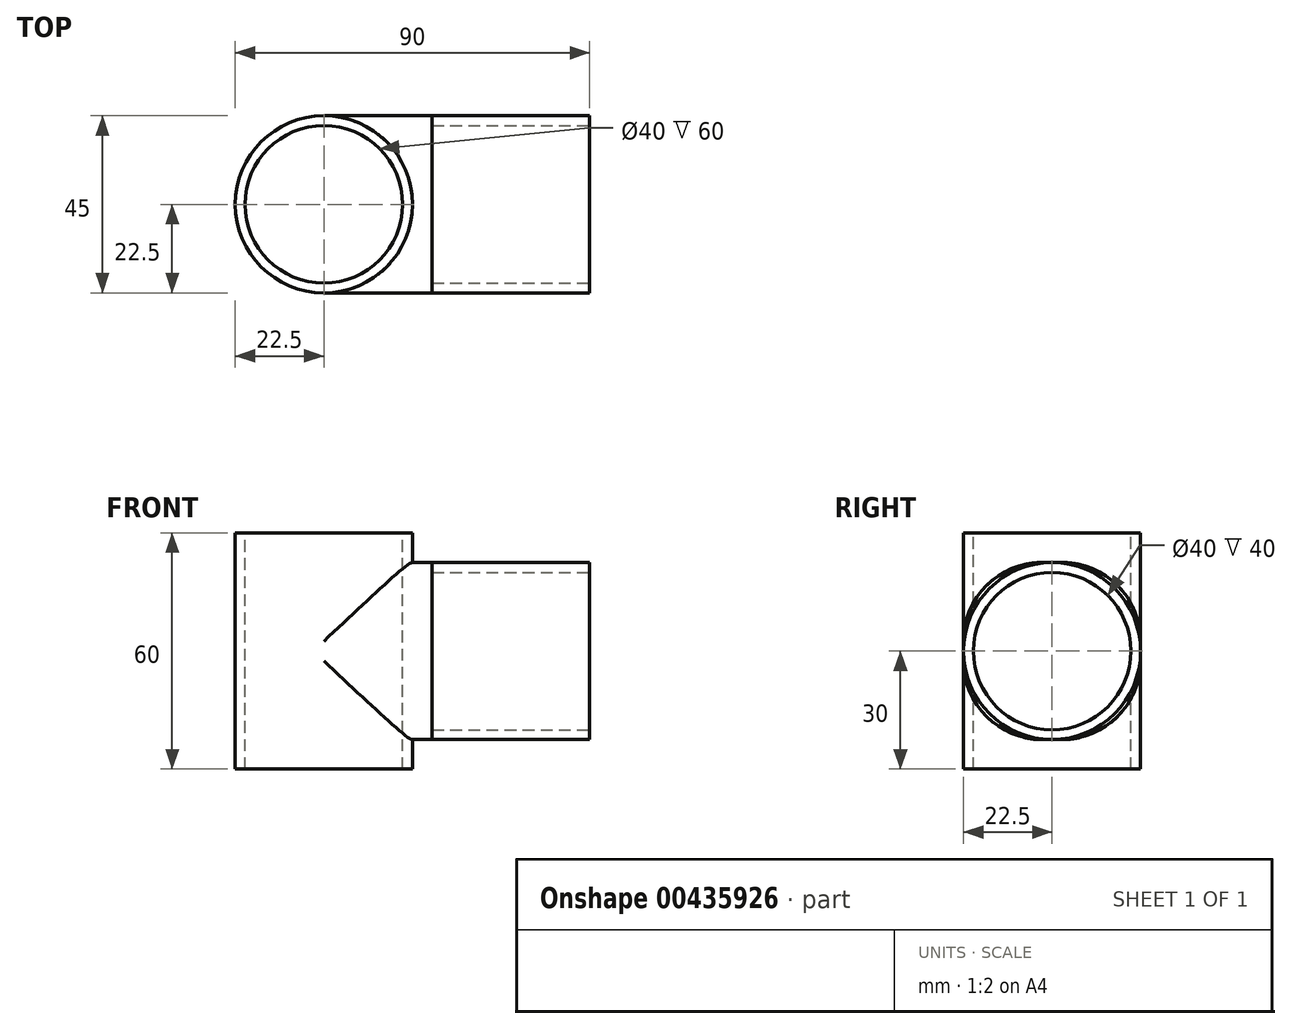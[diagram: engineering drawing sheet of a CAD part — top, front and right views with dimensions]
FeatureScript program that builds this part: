
annotation { "Feature Type Name" : "Feature", "Feature Type Description" : "" }
export const myFeature = defineFeature(function(context is Context, id is Id, definition is map)
    precondition{}
    {
        {
            var Q0;
            Q0=qCreatedBy(makeId("Top.planeOp"),FACE);
            var sketch = newSketch(context, id + "F0", { "sketchPlane" : qUnion([Q0])});
            skCircle(sketch, "E0", {"center": v(0, 0) * mm, "radius": 22.5 * mm});
            skLineSegment(sketch, "E1", {"start": v(0, 22.5) * mm, "end": v(67.5, 22.5) * mm});
            skLineSegment(sketch, "E2", {"start": v(67.5, -22.5) * mm, "end": v(0, -22.5) * mm});
            skLineSegment(sketch, "E3", {"start": v(67.5, 22.5) * mm, "end": v(67.5, -22.5) * mm});
            skSolve(sketch);
        }
        {
            var Q0;
            {var subQ0=sQuery(id+"F0.wireOp",EDGE,"E1");Q0=makeQuery(id+"F0.imprint","IMPRINT",FACE,{"disambiguationData":[TD([[makeQuery(id+"F0.imprint","IMPRINT",EDGE,{"derivedFrom":subQ0}),-1.0]])]});}
            extrude(context, id + "F1", {"entities" : qUnion([Q0]), "endBound" : BoundingType.SYMMETRIC, "depth" : 45 * mm});
        }
        {
            var Q0;
            {var subQ0=sQuery(id+"F0.wireOp",EDGE,"E0");var subQ1=makeQuery(id+"F0.imprint","INTERSECT",VERTEX,{"derivedFrom":[subQ0,sQuery(id+"F0.wireOp",EDGE,"E1")]});Q0=makeQuery(id+"F0.imprint","IMPRINT",FACE,{"disambiguationData":[TD([[makeQuery(id+"F0.imprint","IMPRINT",EDGE,{"disambiguationData":[TD([[subQ1,-1.0]])],"derivedFrom":subQ0}),1.0]])]});}
            extrude(context, id + "F2", {"entities" : qUnion([Q0]), "operationType" : NewBodyOperationType.ADD, "endBound" : BoundingType.SYMMETRIC, "depth" : 60 * mm});
        }
        {
            var Q0;
            Q0=makeQuery(id+"F1.opExtrude","SWEPT_FACE",FACE,{"disambiguationData":[OSD([sQuery(id+"F0.wireOp",EDGE,"E3")])]});
            var sketch = newSketch(context, id + "F3", { "sketchPlane" : qUnion([Q0])});
            skCircle(sketch, "E4", {"center": v(0, 0) * mm, "radius": 22.5 * mm});
            skSolve(sketch);
        }
        {
            var Q0;
            {var subQ0=sQuery(id+"F3.wireOp",EDGE,"E4");var subQ1=sQuery(id+"F0.wireOp",EDGE,"E3");var subQ4=makeQuery(id+"F1.opExtrude","CAP_EDGE",EDGE,{"disambiguationData":[OSD([subQ1])],"isStart":true});var subQ5=makeQuery(id+"F3.imprint","INTERSECT",VERTEX,{"derivedFrom":[subQ4,subQ0]});Q0=makeQuery(id+"F3.imprint","IMPRINT",FACE,{"disambiguationData":[TD([[makeQuery(id+"F3.imprint","IMPRINT",EDGE,{"disambiguationData":[TD([[subQ5,1.0]])],"derivedFrom":subQ0}),-1.0]])]});}
            var Q1;
            {var subQ0=sQuery(id+"F3.wireOp",EDGE,"E4");var subQ1=sQuery(id+"F0.wireOp",EDGE,"E3");var subQ2=makeQuery(id+"F1.opExtrude","CAP_EDGE",EDGE,{"disambiguationData":[OSD([subQ1])],"isStart":false});var subQ3=makeQuery(id+"F3.imprint","INTERSECT",VERTEX,{"derivedFrom":[subQ2,subQ0]});Q1=makeQuery(id+"F3.imprint","IMPRINT",FACE,{"disambiguationData":[TD([[makeQuery(id+"F3.imprint","IMPRINT",EDGE,{"disambiguationData":[TD([[subQ3,-1.0]])],"derivedFrom":subQ0}),-1.0]])]});}
            var Q2;
            {var subQ0=sQuery(id+"F3.wireOp",EDGE,"E4");var subQ1=sQuery(id+"F0.wireOp",EDGE,"E3");var subQ2=makeQuery(id+"F1.opExtrude","CAP_EDGE",EDGE,{"disambiguationData":[OSD([subQ1])],"isStart":false});var subQ3=makeQuery(id+"F3.imprint","INTERSECT",VERTEX,{"derivedFrom":[subQ2,subQ0]});Q2=makeQuery(id+"F3.imprint","IMPRINT",FACE,{"disambiguationData":[TD([[makeQuery(id+"F3.imprint","IMPRINT",EDGE,{"disambiguationData":[TD([[subQ3,1.0]])],"derivedFrom":subQ0}),-1.0]])]});}
            var Q3;
            {var subQ0=sQuery(id+"F3.wireOp",EDGE,"E4");var subQ1=sQuery(id+"F0.wireOp",EDGE,"E3");var subQ4=makeQuery(id+"F1.opExtrude","CAP_EDGE",EDGE,{"disambiguationData":[OSD([subQ1])],"isStart":true});var subQ5=makeQuery(id+"F3.imprint","INTERSECT",VERTEX,{"derivedFrom":[subQ4,subQ0]});Q3=makeQuery(id+"F3.imprint","IMPRINT",FACE,{"disambiguationData":[TD([[makeQuery(id+"F3.imprint","IMPRINT",EDGE,{"disambiguationData":[TD([[subQ5,-1.0]])],"derivedFrom":subQ0}),-1.0]])]});}
            extrude(context, id + "F4", {"entities" : qUnion([Q0, Q1, Q2, Q3]), "operationType" : NewBodyOperationType.REMOVE, "oppositeDirection" : true, "depth" : 40 * mm});
        }
        {
            var Q0;
            Q0=makeQuery(id+"F1.opExtrude","CAP_EDGE",EDGE,{"disambiguationData":[OSD([sQuery(id+"F0.wireOp",EDGE,"E1")])],"isStart":false});
            var Q1;
            Q1=makeQuery(id+"F1.opExtrude","CAP_EDGE",EDGE,{"disambiguationData":[OSD([sQuery(id+"F0.wireOp",EDGE,"E1")])],"isStart":true});
            var Q2;
            Q2=makeQuery(id+"F1.opExtrude","CAP_EDGE",EDGE,{"disambiguationData":[OSD([sQuery(id+"F0.wireOp",EDGE,"E2")])],"isStart":false});
            var Q3;
            Q3=makeQuery(id+"F1.opExtrude","CAP_EDGE",EDGE,{"disambiguationData":[OSD([sQuery(id+"F0.wireOp",EDGE,"E2")])],"isStart":true});
            fillet(context, id + "F5", {"entities" : qUnion([Q0, Q1, Q2, Q3]), "radius" : 20 * mm, "tangentPropagation" : true, "allowEdgeOverflow" : false});
        }
        {
            var Q0;
            Q0=makeQuery(id+"F2.opExtrude","CAP_FACE",FACE,{"disambiguationData":[OSD([sQuery(id+"F0.wireOp",EDGE,"E0")])],"isStart":false});
            var sketch = newSketch(context, id + "F6", { "sketchPlane" : qUnion([Q0])});
            skCircle(sketch, "E5", {"center": v(0, 0) * mm, "radius": 20 * mm});
            skSolve(sketch);
        }
        {
            var Q0;
            Q0=makeQuery(id+"F6.imprint","IMPRINT",FACE,{"disambiguationData":[TD([[makeQuery(id+"F6.imprint","IMPRINT",EDGE,{"derivedFrom":sQuery(id+"F6.wireOp",EDGE,"E5")}),1.0]])]});
            extrude(context, id + "F7", {"entities" : qUnion([Q0]), "operationType" : NewBodyOperationType.REMOVE, "oppositeDirection" : true, "depth" : 100 * mm});
        }
        {
            var Q0;
            Q0=makeQuery(id+"F1.opExtrude","SWEPT_FACE",FACE,{"disambiguationData":[OSD([sQuery(id+"F0.wireOp",EDGE,"E3")])]});
            var sketch = newSketch(context, id + "F8", { "sketchPlane" : qUnion([Q0])});
            skCircle(sketch, "E6", {"center": v(0, 0) * mm, "radius": 20 * mm});
            skSolve(sketch);
        }
        {
            var Q0;
            Q0 = qSketchRegion(id + "F8", true);
            extrude(context, id + "F9", {"entities" : qUnion([Q0]), "operationType" : NewBodyOperationType.REMOVE, "oppositeDirection" : true, "depth" : 40 * mm});
        }
    });
